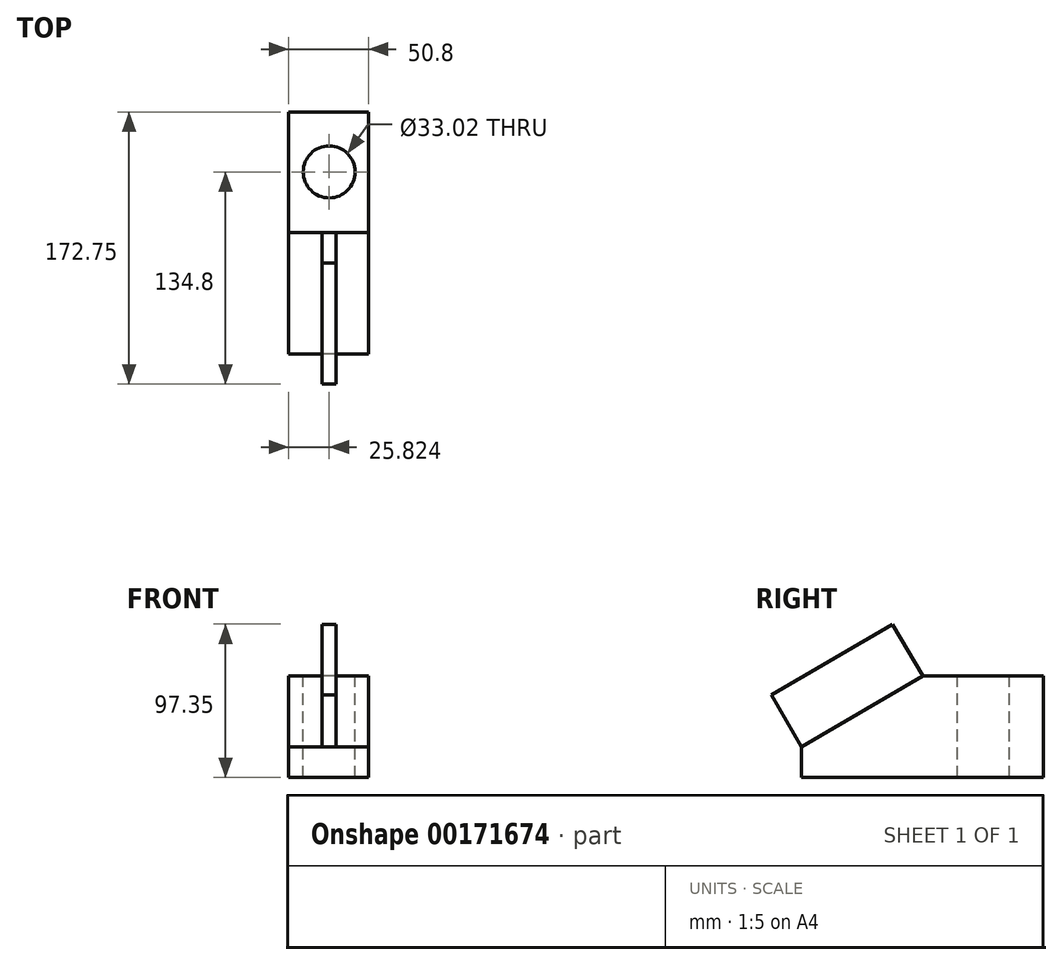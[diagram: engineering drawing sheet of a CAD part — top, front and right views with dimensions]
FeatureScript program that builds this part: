
annotation { "Feature Type Name" : "Feature", "Feature Type Description" : "" }
export const myFeature = defineFeature(function(context is Context, id is Id, definition is map)
    precondition{}
    {
        {
            var Q0;
            Q0=qCreatedBy(makeId("Right.planeOp"),FACE);
            var sketch = newSketch(context, id + "F0", { "sketchPlane" : qUnion([Q0])});
            skLineSegment(sketch, "E0", {"start": v(76.58, 29.22) * mm, "end": v(76.58, -35.25) * mm});
            skLineSegment(sketch, "E1", {"start": v(76.58, -35.25) * mm, "end": v(-76.92, -35.25) * mm});
            skLineSegment(sketch, "E2", {"start": v(76.58, 29.22) * mm, "end": v(0, 29.22) * mm});
            skLineSegment(sketch, "E3", {"start": v(-76.92, -35.25) * mm, "end": v(-76.92, -15.81) * mm});
            skLineSegment(sketch, "E4", {"start": v(-76.92, -15.81) * mm, "end": v(0, 29.22) * mm});
            skLineSegment(sketch, "E5", {"start": v(-76.92, -15.81) * mm, "end": v(0, -15.81) * mm});
            skLineSegment(sketch, "E6", {"start": v(0, -15.81) * mm, "end": v(0, 29.22) * mm});
            skLineSegment(sketch, "E7", {"start": v(-52.36, -15.81) * mm, "end": v(-52.36, -35.25) * mm});
            skLineSegment(sketch, "E8", {"start": v(62.25, 29.22) * mm, "end": v(62.25, -35.25) * mm});
            skLineSegment(sketch, "E9", {"start": v(62.25, -35.25) * mm, "end": v(45.88, -35.25) * mm});
            skLineSegment(sketch, "E10", {"start": v(45.88, -35.25) * mm, "end": v(45.88, 29.22) * mm});
            skLineSegment(sketch, "E11", {"start": v(45.88, 29.22) * mm, "end": v(30.53, 29.22) * mm});
            skLineSegment(sketch, "E12", {"start": v(30.53, 29.22) * mm, "end": v(30.53, -35.25) * mm});
            skSolve(sketch);
        }
        {
            var Q0;
            {var subQ0=sQuery(id+"F0.wireOp",EDGE,"E0");Q0=makeQuery(id+"F0.imprint","IMPRINT",FACE,{"disambiguationData":[TD([[makeQuery(id+"F0.imprint","IMPRINT",EDGE,{"derivedFrom":subQ0}),-1.0]])]});}
            var Q1;
            {var subQ0=sQuery(id+"F0.wireOp",EDGE,"E8");Q1=makeQuery(id+"F0.imprint","IMPRINT",FACE,{"disambiguationData":[TD([[makeQuery(id+"F0.imprint","IMPRINT",EDGE,{"derivedFrom":subQ0}),-1.0]])]});}
            var Q2;
            {var subQ0=sQuery(id+"F0.wireOp",EDGE,"E10");Q2=makeQuery(id+"F0.imprint","IMPRINT",FACE,{"disambiguationData":[TD([[makeQuery(id+"F0.imprint","IMPRINT",EDGE,{"derivedFrom":subQ0}),1.0]])]});}
            var Q3;
            {var subQ0=sQuery(id+"F0.wireOp",EDGE,"E6");Q3=makeQuery(id+"F0.imprint","IMPRINT",FACE,{"disambiguationData":[TD([[makeQuery(id+"F0.imprint","IMPRINT",EDGE,{"derivedFrom":subQ0}),-1.0]])]});}
            var Q4;
            {var subQ0=sQuery(id+"F0.wireOp",EDGE,"E4");Q4=makeQuery(id+"F0.imprint","IMPRINT",FACE,{"disambiguationData":[TD([[makeQuery(id+"F0.imprint","IMPRINT",EDGE,{"derivedFrom":subQ0}),-1.0]])]});}
            var Q5;
            {var subQ0=sQuery(id+"F0.wireOp",EDGE,"E3");Q5=makeQuery(id+"F0.imprint","IMPRINT",FACE,{"disambiguationData":[TD([[makeQuery(id+"F0.imprint","IMPRINT",EDGE,{"derivedFrom":subQ0}),-1.0]])]});}
            extrude(context, id + "F1", {"entities" : qUnion([Q0, Q1, Q2, Q3, Q4, Q5]), "depth" : 50.8 * mm});
        }
        {
            var Q0;
            Q0=makeQuery(id+"F1.opExtrude","SWEPT_FACE",FACE,{"disambiguationData":[OSD([sQuery(id+"F0.wireOp",EDGE,"E4")])]});
            var sketch = newSketch(context, id + "F2", { "sketchPlane" : qUnion([Q0])});
            skLineSegment(sketch, "E13", {"start": v(30.24, 14.76) * mm, "end": v(30.24, -74.37) * mm});
            skLineSegment(sketch, "E14", {"start": v(30.24, -74.37) * mm, "end": v(21.41, -74.37) * mm});
            skLineSegment(sketch, "E15", {"start": v(21.41, -74.37) * mm, "end": v(21.41, 14.76) * mm});
            skLineSegment(sketch, "E16", {"start": v(21.41, -74.37) * mm, "end": v(0, -51.9) * mm});
            skLineSegment(sketch, "E17", {"start": v(0, -51.9) * mm, "end": v(21.41, -74.37) * mm});
            skLineSegment(sketch, "E18", {"start": v(30.24, -74.37) * mm, "end": v(50.8, -51.9) * mm});
            skLineSegment(sketch, "E19", {"start": v(50.8, 14.76) * mm, "end": v(0, 14.76) * mm});
            skCircle(sketch, "E20", {"center": v(25.4, 59.5) * mm, "radius": 19.03 * mm});
            skPoint(sketch, "E20.centerSnap0", {"position": v(25.4, 14.76) * mm});
            skPoint(sketch, "E21", {"position": v(25.4, 40.46) * mm});
            skPoint(sketch, "E22", {"position": v(25.4, 78.52) * mm});
            skSolve(sketch);
        }
        {
            var Q0;
            {var subQ0=sQuery(id+"F2.wireOp",EDGE,"E13");Q0=makeQuery(id+"F2.imprint","IMPRINT",FACE,{"disambiguationData":[TD([[makeQuery(id+"F2.imprint","IMPRINT",EDGE,{"derivedFrom":subQ0}),-1.0]])]});}
            extrude(context, id + "F3", {"entities" : qUnion([Q0]), "operationType" : NewBodyOperationType.ADD, "depth" : 38.1 * mm});
        }
        {
            var Q0;
            Q0=makeQuery(id+"F1.opExtrude","SWEPT_FACE",FACE,{"disambiguationData":[OSD([sQuery(id+"F0.wireOp",EDGE,"E2"),sQuery(id+"F0.wireOp",EDGE,"E11")])]});
            var sketch = newSketch(context, id + "F4", { "sketchPlane" : qUnion([Q0])});
            skPoint(sketch, "E23", {"position": v(25.82, 38.63) * mm});
            skPoint(sketch, "E23.positionSnap0", {"position": v(25.82, 0) * mm});
            skSolve(sketch);
        }
        {
            var Q0;
            Q0=sQuery(id+"F4.wireOp",VERTEX,"E23");
            var Q1;
            Q1=makeQuery(id+"F1.opExtrude","SWEPT_BODY",BODY,{"disambiguationData":[OSD([sQuery(id+"F0.wireOp",EDGE,"E0"),sQuery(id+"F0.wireOp",EDGE,"E1"),sQuery(id+"F0.wireOp",EDGE,"E2"),sQuery(id+"F0.wireOp",EDGE,"E3"),sQuery(id+"F0.wireOp",EDGE,"E4"),sQuery(id+"F0.wireOp",EDGE,"E9"),sQuery(id+"F0.wireOp",EDGE,"E11")])]});
            hole(context, id + "F5", {"style" : HoleStyle.SIMPLE, "endStyle" : HoleEndStyle.THROUGH, "holeDiameter" : 33.02 * mm, "locations" : qUnion([Q0]), "scope" : qUnion([Q1]), "isTappedThrough" : true});
        }
    });
